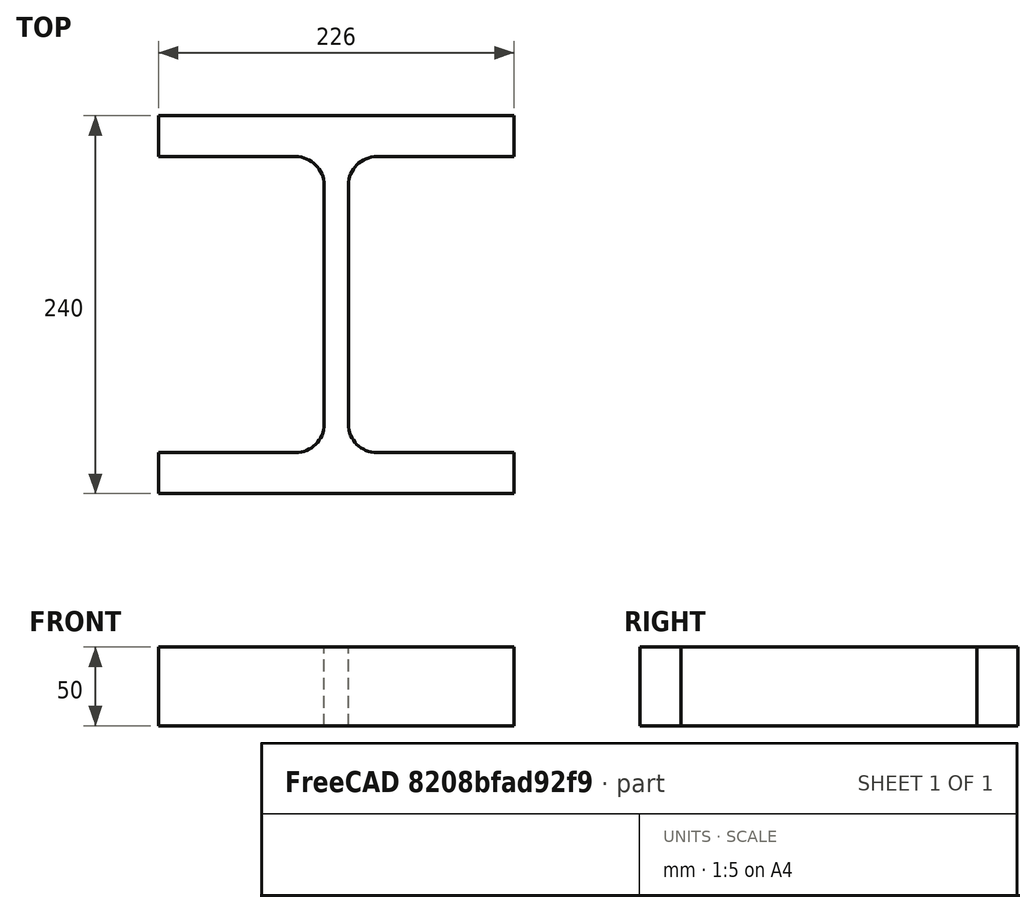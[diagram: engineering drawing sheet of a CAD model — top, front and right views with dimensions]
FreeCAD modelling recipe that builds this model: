
FCSTD DOCUMENT  (FreeCAD 0.15R4671 (Git))
Label: HE-M-Profile 220 DIN1025-4 S235JR
License: All rights reserved
LicenseURL: http://en.wikipedia.org/wiki/All_rights_reserved
objects: Sketcher::SketchObject×1, Part::Extrusion×1
note: 2 computed .brp shape members not serialized (recipe doc carries the construction recipe); baked Part::Feature solids carry a one-line shape summary decoded from their .brp

FEATURE [Sketcher::SketchObject] Sketch
  sketch-geometry (16):
    g0: LineSegment StartX=7.75 StartY=-76 StartZ=0 EndX=7.75 EndY=76 EndZ=0
    g1: LineSegment StartX=25.75 StartY=94 StartZ=0 EndX=113 EndY=94 EndZ=0
    g2: LineSegment StartX=113 StartY=94 StartZ=0 EndX=113 EndY=120 EndZ=0
    g3: LineSegment StartX=113 StartY=120 StartZ=0 EndX=-113 EndY=120 EndZ=0
    g4: LineSegment StartX=-113 StartY=120 StartZ=0 EndX=-113 EndY=94 EndZ=0
    g5: LineSegment StartX=-113 StartY=94 StartZ=0 EndX=-25.75 EndY=94 EndZ=0
    g6: LineSegment StartX=-7.75 StartY=76 StartZ=0 EndX=-7.75 EndY=-76 EndZ=0
    g7: LineSegment StartX=-25.75 StartY=-94 StartZ=0 EndX=-113 EndY=-94 EndZ=0
    g8: LineSegment StartX=-113 StartY=-94 StartZ=0 EndX=-113 EndY=-120 EndZ=0
    g9: LineSegment StartX=-113 StartY=-120 StartZ=0 EndX=113 EndY=-120 EndZ=0
    g10: LineSegment StartX=113 StartY=-120 StartZ=0 EndX=113 EndY=-94 EndZ=0
    g11: LineSegment StartX=113 StartY=-94 StartZ=0 EndX=25.75 EndY=-94 EndZ=0
    g12: ArcOfCircle CenterX=25.75 CenterY=76 CenterZ=0 NormalX=0 NormalY=0 NormalZ=1 Radius=18 StartAngle=1.5708 EndAngle=3.14159
    g13: ArcOfCircle CenterX=25.75 CenterY=-76 CenterZ=0 NormalX=0 NormalY=0 NormalZ=1 Radius=18 StartAngle=3.14159 EndAngle=4.71239
    g14: ArcOfCircle CenterX=-25.75 CenterY=76 CenterZ=0 NormalX=0 NormalY=0 NormalZ=1 Radius=18 StartAngle=0 EndAngle=1.5708
    g15: ArcOfCircle CenterX=-25.75 CenterY=-76 CenterZ=0 NormalX=0 NormalY=0 NormalZ=1 Radius=18 StartAngle=4.71239 EndAngle=6.28319
  constraints (42):
    c: Vertical(g0)
    c: Coincident(g2,g1)
    c: Vertical(g2)
    c: Coincident(g3,g2)
    c: Coincident(g4,g3)
    c: Vertical(g4)
    c: Coincident(g5,g4)
    c: Horizontal(g5)
    c: Vertical(g6)
    c: Horizontal(g7)
    c: Coincident(g8,g7)
    c: Vertical(g8)
    c: Coincident(g9,g8)
    c: Horizontal(g9)
    c: Coincident(g10,g9)
    c: Vertical(g10)
    c: Coincident(g11,g10)
    c: Horizontal(g11)
    c: Tangent(g1,g12) = 1.5708
    c: Tangent(g0,g12) = 1.5708
    c: Tangent(g0,g13) = 1.5708
    c: Tangent(g11,g13) = 1.5708
    c: Tangent(g5,g14) = 1.5708
    c: Tangent(g6,g14) = 1.5708
    c: Tangent(g6,g15) = 1.5708
    c: Tangent(g7,g15) = 1.5708
    c: Equal(g3,g9)
    c: Equal(g2,g4)
    c: Equal(g4,g8)
    c: Equal(g8,g10)
    c: Equal(g12,g14)
    c: Equal(g14,g15)
    c: Equal(g15,g13)
    c: Symmetric(g2,g3,g-2)
    c: Symmetric(g9,g8,g-2)
    c: Symmetric(g0,g6,g-2)
    c: Symmetric(g2,g9,g-1)
    c: DistanceY(g2,g9) = -240
    c: DistanceX(g3) = -226
    c: DistanceX(g0,g6) = -15.5
    c: DistanceY(g2) = 26
    c: Radius(g12) = 18
FEATURE [Part::Extrusion] Extrude  label="HE-M-Profile 220 DIN1025-4 S235JR"
  Base = -> Sketch
  Dir = (0,0,50)
  Solid = true
